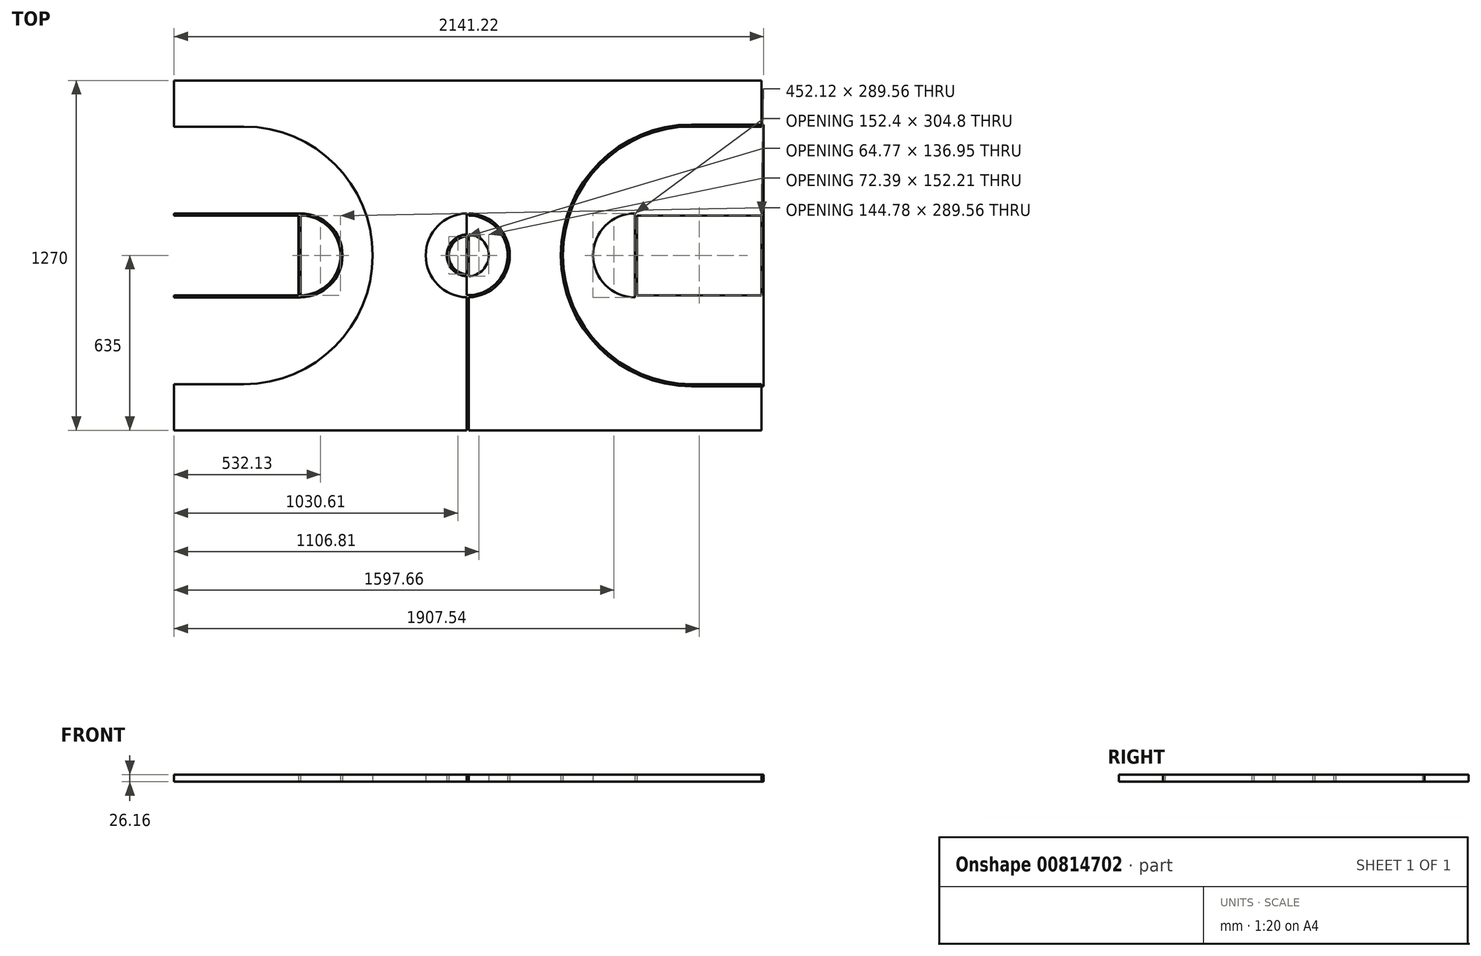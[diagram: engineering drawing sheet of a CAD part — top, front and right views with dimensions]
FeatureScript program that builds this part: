
annotation { "Feature Type Name" : "Feature", "Feature Type Description" : "" }
export const myFeature = defineFeature(function(context is Context, id is Id, definition is map)
    precondition{}
    {
        {
            var Q0;
            Q0=qCreatedBy(makeId("Top.planeOp"),FACE);
            var sketch = newSketch(context, id + "F0", { "sketchPlane" : qUnion([Q0])});
            skLineSegment(sketch, "E0.bottom", {"start": v(-1066.8, -635) * mm, "end": v(1066.8, -635) * mm});
            skLineSegment(sketch, "E0.top", {"start": v(-1066.8, 635) * mm, "end": v(1066.8, 635) * mm});
            skLineSegment(sketch, "E0.left", {"start": v(-1066.8, -635) * mm, "end": v(-1066.8, 635) * mm});
            skLineSegment(sketch, "E0.right", {"start": v(1066.8, -635) * mm, "end": v(1066.8, 635) * mm});
            skPoint(sketch, "E0.middle", {"position": v(0, 0) * mm});
            skLineSegment(sketch, "E1.bottom", {"start": v(-3.81, -635) * mm, "end": v(3.81, -635) * mm});
            skLineSegment(sketch, "E1.top", {"start": v(-3.81, 635) * mm, "end": v(3.81, 635) * mm});
            skLineSegment(sketch, "E1.left", {"start": v(-3.81, -635) * mm, "end": v(-3.81, 635) * mm});
            skLineSegment(sketch, "E1.right", {"start": v(3.81, -635) * mm, "end": v(3.81, 635) * mm});
            skCircle(sketch, "E2", {"center": v(0, 0) * mm, "radius": 152.4 * mm});
            skCircle(sketch, "E3", {"center": v(0, 0) * mm, "radius": 144.78 * mm});
            skCircle(sketch, "E4", {"center": v(0, 0) * mm, "radius": 76.2 * mm});
            skCircle(sketch, "E5", {"center": v(0, 0) * mm, "radius": 68.58 * mm});
            skPoint(sketch, "E6.endSnap0", {"position": v(-1066.8, 0) * mm});
            skLineSegment(sketch, "E7.bottom", {"start": v(-1066.8, -152.4) * mm, "end": v(-607.06, -152.4) * mm});
            skLineSegment(sketch, "E7.top", {"start": v(-1066.8, 152.4) * mm, "end": v(-607.06, 152.4) * mm});
            skLineSegment(sketch, "E7.left", {"start": v(-1066.8, -152.4) * mm, "end": v(-1066.8, 152.4) * mm});
            skLineSegment(sketch, "E7.right", {"start": v(-607.06, -152.4) * mm, "end": v(-607.06, 152.4) * mm});
            skPoint(sketch, "E7.middle", {"position": v(-836.93, 0) * mm});
            skPoint(sketch, "E6.end.orphan", {"position": v(-607.06, 0) * mm});
            skArc(sketch, "E8", {"start": v(-607.06, -152.4) * mm, "mid": v(-454.66, 0) * mm, "end": v(-607.06, 152.4) * mm});
            skLineSegment(sketch, "E9", {"start": v(-1066.8, 635) * mm, "end": v(-1066.8, 474.98) * mm});
            skLineSegment(sketch, "E10", {"start": v(-1066.8, -635) * mm, "end": v(-1066.8, -474.98) * mm});
            skLineSegment(sketch, "E11", {"start": v(-1066.8, 474.98) * mm, "end": v(-812.8, 474.98) * mm});
            skLineSegment(sketch, "E12", {"start": v(-1066.8, -474.98) * mm, "end": v(-812.8, -474.98) * mm});
            skArc(sketch, "E13", {"start": v(-812.8, -474.98) * mm, "mid": v(-337.82, 0) * mm, "end": v(-812.8, 474.98) * mm});
            skLineSegment(sketch, "E14", {"start": v(0, 635) * mm, "end": v(0, -635) * mm});
            skArc(sketch, "E15.MirrorCS", {"start": v(812.8, -474.98) * mm, "mid": v(337.82, 0) * mm, "end": v(812.8, 474.98) * mm});
            skArc(sketch, "E16.MirrorCS", {"start": v(607.06, -152.4) * mm, "mid": v(454.66, 0) * mm, "end": v(607.06, 152.4) * mm});
            skLineSegment(sketch, "E17.MirrorCS", {"start": v(607.06, -152.4) * mm, "end": v(607.06, 152.4) * mm});
            skLineSegment(sketch, "E18.MirrorCS", {"start": v(1066.8, -474.98) * mm, "end": v(812.8, -474.98) * mm});
            skLineSegment(sketch, "E19.MirrorCS", {"start": v(1066.8, 474.98) * mm, "end": v(812.8, 474.98) * mm});
            skLineSegment(sketch, "E20.MirrorCS", {"start": v(1066.8, 152.4) * mm, "end": v(607.06, 152.4) * mm});
            skLineSegment(sketch, "E21.MirrorCS", {"start": v(1066.8, -152.4) * mm, "end": v(607.06, -152.4) * mm});
            skLineSegment(sketch, "E22", {"start": v(-1066.8, 474.98) * mm, "end": v(-1066.8, 467.36) * mm});
            skLineSegment(sketch, "E23", {"start": v(-1066.8, 467.36) * mm, "end": v(-812.8, 467.36) * mm});
            skLineSegment(sketch, "E24", {"start": v(-812.8, 467.36) * mm, "end": v(-812.8, 474.98) * mm});
            skLineSegment(sketch, "E25", {"start": v(-1066.8, -474.98) * mm, "end": v(-1066.8, -467.36) * mm});
            skLineSegment(sketch, "E26", {"start": v(-1066.8, -467.36) * mm, "end": v(-812.8, -467.36) * mm});
            skArc(sketch, "E27", {"start": v(-812.8, -467.36) * mm, "mid": v(-345.44, 0) * mm, "end": v(-812.8, 467.36) * mm});
            skLineSegment(sketch, "E28", {"start": v(-1066.8, 152.4) * mm, "end": v(-1066.8, 144.78) * mm});
            skLineSegment(sketch, "E29", {"start": v(-1066.8, 144.78) * mm, "end": v(-607.06, 144.78) * mm});
            skLineSegment(sketch, "E30", {"start": v(-1066.8, -152.4) * mm, "end": v(-1066.8, -144.78) * mm});
            skLineSegment(sketch, "E31", {"start": v(-1066.8, -144.78) * mm, "end": v(-607.06, -144.78) * mm});
            skLineSegment(sketch, "E32", {"start": v(-607.06, 152.4) * mm, "end": v(-614.68, 152.4) * mm});
            skLineSegment(sketch, "E33", {"start": v(-614.68, 152.4) * mm, "end": v(-614.68, -152.4) * mm});
            skLineSegment(sketch, "E34", {"start": v(-614.68, -152.4) * mm, "end": v(-607.06, -152.4) * mm});
            skArc(sketch, "E35", {"start": v(-607.06, -144.78) * mm, "mid": v(-462.28, 0) * mm, "end": v(-607.06, 144.78) * mm});
            skArc(sketch, "E36.MirrorCS", {"start": v(812.8, -467.36) * mm, "mid": v(345.44, 0) * mm, "end": v(812.8, 467.36) * mm});
            skArc(sketch, "E37.MirrorCS", {"start": v(607.06, -144.78) * mm, "mid": v(462.28, 0) * mm, "end": v(607.06, 144.78) * mm});
            skLineSegment(sketch, "E38.MirrorCS", {"start": v(614.68, 152.4) * mm, "end": v(614.68, -152.4) * mm});
            skLineSegment(sketch, "E39.MirrorCS", {"start": v(1066.8, -144.78) * mm, "end": v(607.06, -144.78) * mm});
            skLineSegment(sketch, "E40.MirrorCS", {"start": v(1066.8, 144.78) * mm, "end": v(607.06, 144.78) * mm});
            skLineSegment(sketch, "E41.MirrorCS", {"start": v(1066.8, -467.36) * mm, "end": v(812.8, -467.36) * mm});
            skLineSegment(sketch, "E42.MirrorCS", {"start": v(1066.8, 467.36) * mm, "end": v(812.8, 467.36) * mm});
            skLineSegment(sketch, "E43", {"start": v(1066.8, 474.98) * mm, "end": v(1074.42, 474.98) * mm});
            skLineSegment(sketch, "E44", {"start": v(1074.42, 474.98) * mm, "end": v(1074.42, -474.98) * mm});
            skLineSegment(sketch, "E45", {"start": v(1074.42, -474.98) * mm, "end": v(1066.8, -474.98) * mm});
            skLineSegment(sketch, "E46.MirrorCS", {"start": v(-1074.42, -474.98) * mm, "end": v(-1066.8, -474.98) * mm});
            skLineSegment(sketch, "E47.MirrorCS", {"start": v(-1074.42, 474.98) * mm, "end": v(-1074.42, -474.98) * mm});
            skLineSegment(sketch, "E48.MirrorCS", {"start": v(-1066.8, 474.98) * mm, "end": v(-1074.42, 474.98) * mm});
            skSolve(sketch);
        }
        {
            var Q0;
            Q0=makeQuery(id+"F0.imprint","IMPRINT",FACE,{"disambiguationData":[TD([[makeQuery(id+"F0.imprint","IMPRINT",EDGE,{"derivedFrom":sQuery(id+"F0.wireOp",EDGE,"E12")}),1.0]])]});
            var Q1;
            Q1=makeQuery(id+"F0.imprint","IMPRINT",FACE,{"disambiguationData":[TD([[makeQuery(id+"F0.imprint","IMPRINT",EDGE,{"derivedFrom":sQuery(id+"F0.wireOp",EDGE,"E11")}),-1.0]])]});
            var Q2;
            {var subQ1=sQuery(id+"F0.wireOp",EDGE,"E29");var subQ6=sQuery(id+"F0.wireOp",EDGE,"E33");var subQ7=makeQuery(id+"F0.imprint","INTERSECT",VERTEX,{"derivedFrom":[subQ1,subQ6]});Q2=makeQuery(id+"F0.imprint","IMPRINT",FACE,{"disambiguationData":[TD([[makeQuery(id+"F0.imprint","IMPRINT",EDGE,{"disambiguationData":[TD([[subQ7,-1.0]])],"derivedFrom":subQ6}),1.0]])]});}
            var Q3;
            {var subQ0=sQuery(id+"F0.wireOp",EDGE,"E7.top");Q3=makeQuery(id+"F0.imprint","IMPRINT",FACE,{"disambiguationData":[TD([[makeQuery(id+"F0.imprint","IMPRINT",EDGE,{"derivedFrom":subQ0}),-1.0]])]});}
            var Q4;
            {var subQ0=sQuery(id+"F0.wireOp",EDGE,"E32");Q4=makeQuery(id+"F0.imprint","IMPRINT",FACE,{"disambiguationData":[TD([[makeQuery(id+"F0.imprint","IMPRINT",EDGE,{"derivedFrom":subQ0}),1.0]])]});}
            var Q5;
            {var subQ0=sQuery(id+"F0.wireOp",EDGE,"E8");Q5=makeQuery(id+"F0.imprint","IMPRINT",FACE,{"disambiguationData":[TD([[makeQuery(id+"F0.imprint","IMPRINT",EDGE,{"derivedFrom":subQ0}),1.0]])]});}
            var Q6;
            {var subQ0=sQuery(id+"F0.wireOp",EDGE,"E7.bottom");Q6=makeQuery(id+"F0.imprint","IMPRINT",FACE,{"disambiguationData":[TD([[makeQuery(id+"F0.imprint","IMPRINT",EDGE,{"derivedFrom":subQ0}),1.0]])]});}
            var Q7;
            {var subQ0=sQuery(id+"F0.wireOp",EDGE,"E34");Q7=makeQuery(id+"F0.imprint","IMPRINT",FACE,{"disambiguationData":[TD([[makeQuery(id+"F0.imprint","IMPRINT",EDGE,{"derivedFrom":subQ0}),1.0]])]});}
            var Q8;
            {var subQ0=sQuery(id+"F0.wireOp",EDGE,"E4");var subQ1=sQuery(id+"F0.wireOp",EDGE,"E1.left");var subQ2=makeQuery(id+"F0.imprint","INTERSECT",VERTEX,{"disambiguationData":[OD(0.0)],"derivedFrom":[subQ1,subQ0]});Q8=makeQuery(id+"F0.imprint","IMPRINT",FACE,{"disambiguationData":[TD([[makeQuery(id+"F0.imprint","IMPRINT",EDGE,{"disambiguationData":[TD([[subQ2,-1.0]])],"derivedFrom":subQ1}),1.0]])]});}
            var Q9;
            {var subQ0=sQuery(id+"F0.wireOp",EDGE,"E4");var subQ1=sQuery(id+"F0.wireOp",EDGE,"E1.right");var subQ2=makeQuery(id+"F0.imprint","INTERSECT",VERTEX,{"disambiguationData":[OD(0.0)],"derivedFrom":[subQ1,subQ0]});Q9=makeQuery(id+"F0.imprint","IMPRINT",FACE,{"disambiguationData":[TD([[makeQuery(id+"F0.imprint","IMPRINT",EDGE,{"disambiguationData":[TD([[subQ2,-1.0]])],"derivedFrom":subQ1}),-1.0]])]});}
            var Q10;
            {var subQ0=sQuery(id+"F0.wireOp",EDGE,"E5");var subQ1=sQuery(id+"F0.wireOp",EDGE,"E1.right");var subQ2=makeQuery(id+"F0.imprint","INTERSECT",VERTEX,{"disambiguationData":[OD(1.0)],"derivedFrom":[subQ1,subQ0]});Q10=makeQuery(id+"F0.imprint","IMPRINT",FACE,{"disambiguationData":[TD([[makeQuery(id+"F0.imprint","IMPRINT",EDGE,{"disambiguationData":[TD([[subQ2,-1.0]])],"derivedFrom":subQ1}),1.0]])]});}
            var Q11;
            {var subQ0=sQuery(id+"F0.wireOp",EDGE,"E5");var subQ1=sQuery(id+"F0.wireOp",EDGE,"E1.left");var subQ2=makeQuery(id+"F0.imprint","INTERSECT",VERTEX,{"disambiguationData":[OD(1.0)],"derivedFrom":[subQ1,subQ0]});Q11=makeQuery(id+"F0.imprint","IMPRINT",FACE,{"disambiguationData":[TD([[makeQuery(id+"F0.imprint","IMPRINT",EDGE,{"disambiguationData":[TD([[subQ2,-1.0]])],"derivedFrom":subQ1}),-1.0]])]});}
            var Q12;
            {var subQ0=sQuery(id+"F0.wireOp",EDGE,"E2");var subQ1=sQuery(id+"F0.wireOp",EDGE,"E1.left");var subQ2=makeQuery(id+"F0.imprint","INTERSECT",VERTEX,{"disambiguationData":[OD(0.0)],"derivedFrom":[subQ1,subQ0]});Q12=makeQuery(id+"F0.imprint","IMPRINT",FACE,{"disambiguationData":[TD([[makeQuery(id+"F0.imprint","IMPRINT",EDGE,{"disambiguationData":[TD([[subQ2,-1.0]])],"derivedFrom":subQ1}),1.0]])]});}
            var Q13;
            {var subQ0=sQuery(id+"F0.wireOp",EDGE,"E3");var subQ1=sQuery(id+"F0.wireOp",EDGE,"E1.left");var subQ2=makeQuery(id+"F0.imprint","INTERSECT",VERTEX,{"disambiguationData":[OD(1.0)],"derivedFrom":[subQ1,subQ0]});Q13=makeQuery(id+"F0.imprint","IMPRINT",FACE,{"disambiguationData":[TD([[makeQuery(id+"F0.imprint","IMPRINT",EDGE,{"disambiguationData":[TD([[subQ2,-1.0]])],"derivedFrom":subQ1}),-1.0]])]});}
            var Q14;
            {var subQ0=sQuery(id+"F0.wireOp",EDGE,"E3");var subQ1=sQuery(id+"F0.wireOp",EDGE,"E1.right");var subQ2=makeQuery(id+"F0.imprint","INTERSECT",VERTEX,{"disambiguationData":[OD(1.0)],"derivedFrom":[subQ1,subQ0]});Q14=makeQuery(id+"F0.imprint","IMPRINT",FACE,{"disambiguationData":[TD([[makeQuery(id+"F0.imprint","IMPRINT",EDGE,{"disambiguationData":[TD([[subQ2,-1.0]])],"derivedFrom":subQ1}),1.0]])]});}
            var Q15;
            {var subQ0=sQuery(id+"F0.wireOp",EDGE,"E2");var subQ1=sQuery(id+"F0.wireOp",EDGE,"E1.right");var subQ2=makeQuery(id+"F0.imprint","INTERSECT",VERTEX,{"disambiguationData":[OD(0.0)],"derivedFrom":[subQ1,subQ0]});Q15=makeQuery(id+"F0.imprint","IMPRINT",FACE,{"disambiguationData":[TD([[makeQuery(id+"F0.imprint","IMPRINT",EDGE,{"disambiguationData":[TD([[subQ2,-1.0]])],"derivedFrom":subQ1}),-1.0]])]});}
            var Q16;
            {var subQ0=sQuery(id+"F0.wireOp",EDGE,"E4");var subQ1=sQuery(id+"F0.wireOp",EDGE,"E1.left");var subQ2=makeQuery(id+"F0.imprint","INTERSECT",VERTEX,{"disambiguationData":[OD(0.0)],"derivedFrom":[subQ1,subQ0]});Q16=makeQuery(id+"F0.imprint","IMPRINT",FACE,{"disambiguationData":[TD([[makeQuery(id+"F0.imprint","IMPRINT",EDGE,{"disambiguationData":[TD([[subQ2,-1.0]])],"derivedFrom":subQ1}),-1.0]])]});}
            var Q17;
            {var subQ0=sQuery(id+"F0.wireOp",EDGE,"E4");var subQ1=sQuery(id+"F0.wireOp",EDGE,"E1.right");var subQ2=makeQuery(id+"F0.imprint","INTERSECT",VERTEX,{"disambiguationData":[OD(0.0)],"derivedFrom":[subQ1,subQ0]});Q17=makeQuery(id+"F0.imprint","IMPRINT",FACE,{"disambiguationData":[TD([[makeQuery(id+"F0.imprint","IMPRINT",EDGE,{"disambiguationData":[TD([[subQ2,-1.0]])],"derivedFrom":subQ1}),1.0]])]});}
            var Q18;
            {var subQ0=sQuery(id+"F0.wireOp",EDGE,"E2");var subQ1=sQuery(id+"F0.wireOp",EDGE,"E1.left");var subQ2=makeQuery(id+"F0.imprint","INTERSECT",VERTEX,{"disambiguationData":[OD(0.0)],"derivedFrom":[subQ1,subQ0]});Q18=makeQuery(id+"F0.imprint","IMPRINT",FACE,{"disambiguationData":[TD([[makeQuery(id+"F0.imprint","IMPRINT",EDGE,{"disambiguationData":[TD([[subQ2,-1.0]])],"derivedFrom":subQ1}),-1.0]])]});}
            var Q19;
            {var subQ0=sQuery(id+"F0.wireOp",EDGE,"E2");var subQ1=sQuery(id+"F0.wireOp",EDGE,"E1.right");var subQ2=makeQuery(id+"F0.imprint","INTERSECT",VERTEX,{"disambiguationData":[OD(0.0)],"derivedFrom":[subQ1,subQ0]});Q19=makeQuery(id+"F0.imprint","IMPRINT",FACE,{"disambiguationData":[TD([[makeQuery(id+"F0.imprint","IMPRINT",EDGE,{"disambiguationData":[TD([[subQ2,-1.0]])],"derivedFrom":subQ1}),1.0]])]});}
            var Q20;
            Q20=makeQuery(id+"F0.imprint","IMPRINT",FACE,{"disambiguationData":[TD([[makeQuery(id+"F0.imprint","IMPRINT",EDGE,{"derivedFrom":sQuery(id+"F0.wireOp",EDGE,"E15.MirrorCS")}),-1.0]])]});
            var Q21;
            {var subQ0=sQuery(id+"F0.wireOp",EDGE,"E20.MirrorCS");var subQ1=sQuery(id+"F0.wireOp",EDGE,"E0.right");var subQ2=makeQuery(id+"F0.imprint","INTERSECT",VERTEX,{"derivedFrom":[subQ1,subQ0]});Q21=makeQuery(id+"F0.imprint","IMPRINT",FACE,{"disambiguationData":[TD([[makeQuery(id+"F0.imprint","IMPRINT",EDGE,{"disambiguationData":[TD([[subQ2,1.0]])],"derivedFrom":subQ1}),1.0]])]});}
            var Q22;
            {var subQ0=sQuery(id+"F0.wireOp",EDGE,"E20.MirrorCS");var subQ5=sQuery(id+"F0.wireOp",EDGE,"E38.MirrorCS");var subQ6=makeQuery(id+"F0.imprint","INTERSECT",VERTEX,{"derivedFrom":[subQ0,subQ5]});Q22=makeQuery(id+"F0.imprint","IMPRINT",FACE,{"disambiguationData":[TD([[makeQuery(id+"F0.imprint","IMPRINT",EDGE,{"disambiguationData":[TD([[subQ6,-1.0]])],"derivedFrom":subQ5}),-1.0]])]});}
            var Q23;
            {var subQ4=sQuery(id+"F0.wireOp",EDGE,"E40.MirrorCS");var subQ6=sQuery(id+"F0.wireOp",EDGE,"E38.MirrorCS");var subQ7=makeQuery(id+"F0.imprint","INTERSECT",VERTEX,{"derivedFrom":[subQ6,subQ4]});Q23=makeQuery(id+"F0.imprint","IMPRINT",FACE,{"disambiguationData":[TD([[makeQuery(id+"F0.imprint","IMPRINT",EDGE,{"disambiguationData":[TD([[subQ7,-1.0]])],"derivedFrom":subQ6}),-1.0]])]});}
            var Q24;
            {var subQ0=sQuery(id+"F0.wireOp",EDGE,"E16.MirrorCS");Q24=makeQuery(id+"F0.imprint","IMPRINT",FACE,{"disambiguationData":[TD([[makeQuery(id+"F0.imprint","IMPRINT",EDGE,{"derivedFrom":subQ0}),-1.0]])]});}
            var Q25;
            {var subQ0=sQuery(id+"F0.wireOp",EDGE,"E21.MirrorCS");var subQ1=sQuery(id+"F0.wireOp",EDGE,"E0.right");var subQ2=makeQuery(id+"F0.imprint","INTERSECT",VERTEX,{"derivedFrom":[subQ1,subQ0]});Q25=makeQuery(id+"F0.imprint","IMPRINT",FACE,{"disambiguationData":[TD([[makeQuery(id+"F0.imprint","IMPRINT",EDGE,{"disambiguationData":[TD([[subQ2,-1.0]])],"derivedFrom":subQ1}),1.0]])]});}
            var Q26;
            {var subQ0=sQuery(id+"F0.wireOp",EDGE,"E21.MirrorCS");var subQ5=sQuery(id+"F0.wireOp",EDGE,"E38.MirrorCS");var subQ6=makeQuery(id+"F0.imprint","INTERSECT",VERTEX,{"derivedFrom":[subQ0,subQ5]});Q26=makeQuery(id+"F0.imprint","IMPRINT",FACE,{"disambiguationData":[TD([[makeQuery(id+"F0.imprint","IMPRINT",EDGE,{"disambiguationData":[TD([[subQ6,1.0]])],"derivedFrom":subQ5}),-1.0]])]});}
            var Q27;
            {var subQ8=sQuery(id+"F0.wireOp",EDGE,"E43");Q27=makeQuery(id+"F0.imprint","IMPRINT",FACE,{"disambiguationData":[TD([[makeQuery(id+"F0.imprint","IMPRINT",EDGE,{"derivedFrom":subQ8}),-1.0]])]});}
            var Q28;
            Q28=makeQuery(id+"F0.imprint","IMPRINT",FACE,{"disambiguationData":[TD([[makeQuery(id+"F0.imprint","IMPRINT",EDGE,{"derivedFrom":sQuery(id+"F0.wireOp",EDGE,"E7.left")}),1.0]])]});
            var Q29;
            {var subQ0=sQuery(id+"F0.wireOp",EDGE,"E1.left");var subQ5=sQuery(id+"F0.wireOp",EDGE,"E2");var subQ6=makeQuery(id+"F0.imprint","INTERSECT",VERTEX,{"disambiguationData":[OD(1.0)],"derivedFrom":[subQ0,subQ5]});Q29=makeQuery(id+"F0.imprint","IMPRINT",FACE,{"disambiguationData":[TD([[makeQuery(id+"F0.imprint","IMPRINT",EDGE,{"disambiguationData":[TD([[subQ6,1.0]])],"derivedFrom":subQ5}),-1.0]])]});}
            var Q30;
            {var subQ0=sQuery(id+"F0.wireOp",EDGE,"E1.right");var subQ5=sQuery(id+"F0.wireOp",EDGE,"E2");var subQ7=makeQuery(id+"F0.imprint","INTERSECT",VERTEX,{"disambiguationData":[OD(1.0)],"derivedFrom":[subQ0,subQ5]});Q30=makeQuery(id+"F0.imprint","IMPRINT",FACE,{"disambiguationData":[TD([[makeQuery(id+"F0.imprint","IMPRINT",EDGE,{"disambiguationData":[TD([[subQ7,-1.0]])],"derivedFrom":subQ5}),-1.0]])]});}
            var Q31;
            {var subQ0=sQuery(id+"F0.wireOp",EDGE,"E4");var subQ1=sQuery(id+"F0.wireOp",EDGE,"E1.left");var subQ2=makeQuery(id+"F0.imprint","INTERSECT",VERTEX,{"disambiguationData":[OD(1.0)],"derivedFrom":[subQ1,subQ0]});Q31=makeQuery(id+"F0.imprint","IMPRINT",FACE,{"disambiguationData":[TD([[makeQuery(id+"F0.imprint","IMPRINT",EDGE,{"disambiguationData":[TD([[subQ2,-1.0]])],"derivedFrom":subQ1}),-1.0]])]});}
            var Q32;
            {var subQ0=sQuery(id+"F0.wireOp",EDGE,"E4");var subQ1=sQuery(id+"F0.wireOp",EDGE,"E1.right");var subQ2=makeQuery(id+"F0.imprint","INTERSECT",VERTEX,{"disambiguationData":[OD(1.0)],"derivedFrom":[subQ1,subQ0]});Q32=makeQuery(id+"F0.imprint","IMPRINT",FACE,{"disambiguationData":[TD([[makeQuery(id+"F0.imprint","IMPRINT",EDGE,{"disambiguationData":[TD([[subQ2,-1.0]])],"derivedFrom":subQ1}),1.0]])]});}
            var Q33;
            {var subQ0=sQuery(id+"F0.wireOp",EDGE,"E5");var subQ1=sQuery(id+"F0.wireOp",EDGE,"E1.left");var subQ2=makeQuery(id+"F0.imprint","INTERSECT",VERTEX,{"disambiguationData":[OD(0.0)],"derivedFrom":[subQ1,subQ0]});Q33=makeQuery(id+"F0.imprint","IMPRINT",FACE,{"disambiguationData":[TD([[makeQuery(id+"F0.imprint","IMPRINT",EDGE,{"disambiguationData":[TD([[subQ2,-1.0]])],"derivedFrom":subQ1}),-1.0]])]});}
            var Q34;
            {var subQ0=sQuery(id+"F0.wireOp",EDGE,"E5");var subQ1=sQuery(id+"F0.wireOp",EDGE,"E1.right");var subQ2=makeQuery(id+"F0.imprint","INTERSECT",VERTEX,{"disambiguationData":[OD(0.0)],"derivedFrom":[subQ1,subQ0]});Q34=makeQuery(id+"F0.imprint","IMPRINT",FACE,{"disambiguationData":[TD([[makeQuery(id+"F0.imprint","IMPRINT",EDGE,{"disambiguationData":[TD([[subQ2,-1.0]])],"derivedFrom":subQ1}),1.0]])]});}
            var Q35;
            {var subQ0=sQuery(id+"F0.wireOp",EDGE,"E3");var subQ1=sQuery(id+"F0.wireOp",EDGE,"E1.left");var subQ2=makeQuery(id+"F0.imprint","INTERSECT",VERTEX,{"disambiguationData":[OD(0.0)],"derivedFrom":[subQ1,subQ0]});Q35=makeQuery(id+"F0.imprint","IMPRINT",FACE,{"disambiguationData":[TD([[makeQuery(id+"F0.imprint","IMPRINT",EDGE,{"disambiguationData":[TD([[subQ2,-1.0]])],"derivedFrom":subQ1}),-1.0]])]});}
            var Q36;
            {var subQ0=sQuery(id+"F0.wireOp",EDGE,"E3");var subQ1=sQuery(id+"F0.wireOp",EDGE,"E1.right");var subQ2=makeQuery(id+"F0.imprint","INTERSECT",VERTEX,{"disambiguationData":[OD(0.0)],"derivedFrom":[subQ1,subQ0]});Q36=makeQuery(id+"F0.imprint","IMPRINT",FACE,{"disambiguationData":[TD([[makeQuery(id+"F0.imprint","IMPRINT",EDGE,{"disambiguationData":[TD([[subQ2,-1.0]])],"derivedFrom":subQ1}),1.0]])]});}
            var Q37;
            {var subQ0=sQuery(id+"F0.wireOp",EDGE,"E1.left");var subQ5=sQuery(id+"F0.wireOp",EDGE,"E2");var subQ6=makeQuery(id+"F0.imprint","INTERSECT",VERTEX,{"disambiguationData":[OD(0.0)],"derivedFrom":[subQ0,subQ5]});Q37=makeQuery(id+"F0.imprint","IMPRINT",FACE,{"disambiguationData":[TD([[makeQuery(id+"F0.imprint","IMPRINT",EDGE,{"disambiguationData":[TD([[subQ6,-1.0]])],"derivedFrom":subQ5}),-1.0]])]});}
            var Q38;
            {var subQ0=sQuery(id+"F0.wireOp",EDGE,"E1.right");var subQ5=sQuery(id+"F0.wireOp",EDGE,"E2");var subQ6=makeQuery(id+"F0.imprint","INTERSECT",VERTEX,{"disambiguationData":[OD(0.0)],"derivedFrom":[subQ0,subQ5]});Q38=makeQuery(id+"F0.imprint","IMPRINT",FACE,{"disambiguationData":[TD([[makeQuery(id+"F0.imprint","IMPRINT",EDGE,{"disambiguationData":[TD([[subQ6,1.0]])],"derivedFrom":subQ5}),-1.0]])]});}
            extrude(context, id + "F1", {"entities" : qUnion([Q0, Q1, Q2, Q3, Q4, Q5, Q6, Q7, Q8, Q9, Q10, Q11, Q12, Q13, Q14, Q15, Q16, Q17, Q18, Q19, Q20, Q21, Q22, Q23, Q24, Q25, Q26, Q27, Q28, Q29, Q30, Q31, Q32, Q33, Q34, Q35, Q36, Q37, Q38]), "depth" : 0.76 * mm, "offsetDistance" : 25.4 * mm});
        }
        {
            var Q0;
            Q0=makeQuery(id+"F1.opExtrude","CAP_FACE",FACE,{"disambiguationData":[OSD([sQuery(id+"F0.wireOp",EDGE,"E0.left"),sQuery(id+"F0.wireOp",EDGE,"E7.bottom"),sQuery(id+"F0.wireOp",EDGE,"E7.top"),sQuery(id+"F0.wireOp",EDGE,"E7.left"),sQuery(id+"F0.wireOp",EDGE,"E7.right"),sQuery(id+"F0.wireOp",EDGE,"E8"),sQuery(id+"F0.wireOp",EDGE,"E11"),sQuery(id+"F0.wireOp",EDGE,"E12"),sQuery(id+"F0.wireOp",EDGE,"E13"),sQuery(id+"F0.wireOp",EDGE,"E23"),sQuery(id+"F0.wireOp",EDGE,"E26"),sQuery(id+"F0.wireOp",EDGE,"E27"),sQuery(id+"F0.wireOp",EDGE,"E29"),sQuery(id+"F0.wireOp",EDGE,"E31"),sQuery(id+"F0.wireOp",EDGE,"E32"),sQuery(id+"F0.wireOp",EDGE,"E33"),sQuery(id+"F0.wireOp",EDGE,"E34"),sQuery(id+"F0.wireOp",EDGE,"E35"),sQuery(id+"F0.wireOp",EDGE,"E46.MirrorCS"),sQuery(id+"F0.wireOp",EDGE,"E47.MirrorCS"),sQuery(id+"F0.wireOp",EDGE,"E48.MirrorCS")])],"isStart":false});
            extrude(context, id + "F2", {"entities" : qUnion([Q0]), "operationType" : NewBodyOperationType.ADD, "depth" : 25.4 * mm, "offsetDistance" : 25.4 * mm});
        }
        {
            var Q0;
            Q0=makeQuery(id+"F1.opExtrude","CAP_FACE",FACE,{"disambiguationData":[OSD([sQuery(id+"F0.wireOp",EDGE,"E1.bottom"),sQuery(id+"F0.wireOp",EDGE,"E1.top"),sQuery(id+"F0.wireOp",EDGE,"E1.left"),sQuery(id+"F0.wireOp",EDGE,"E1.right"),sQuery(id+"F0.wireOp",EDGE,"E2"),sQuery(id+"F0.wireOp",EDGE,"E3"),sQuery(id+"F0.wireOp",EDGE,"E4"),sQuery(id+"F0.wireOp",EDGE,"E5")])],"isStart":false});
            extrude(context, id + "F3", {"entities" : qUnion([Q0]), "operationType" : NewBodyOperationType.ADD, "depth" : 25.4 * mm, "offsetDistance" : 25.4 * mm});
        }
        {
            var Q0;
            Q0=makeQuery(id+"F1.opExtrude","CAP_FACE",FACE,{"disambiguationData":[OSD([sQuery(id+"F0.wireOp",EDGE,"E0.right"),sQuery(id+"F0.wireOp",EDGE,"E15.MirrorCS"),sQuery(id+"F0.wireOp",EDGE,"E16.MirrorCS"),sQuery(id+"F0.wireOp",EDGE,"E17.MirrorCS"),sQuery(id+"F0.wireOp",EDGE,"E18.MirrorCS"),sQuery(id+"F0.wireOp",EDGE,"E19.MirrorCS"),sQuery(id+"F0.wireOp",EDGE,"E20.MirrorCS"),sQuery(id+"F0.wireOp",EDGE,"E21.MirrorCS"),sQuery(id+"F0.wireOp",EDGE,"E36.MirrorCS"),sQuery(id+"F0.wireOp",EDGE,"E37.MirrorCS"),sQuery(id+"F0.wireOp",EDGE,"E38.MirrorCS"),sQuery(id+"F0.wireOp",EDGE,"E39.MirrorCS"),sQuery(id+"F0.wireOp",EDGE,"E40.MirrorCS"),sQuery(id+"F0.wireOp",EDGE,"E41.MirrorCS"),sQuery(id+"F0.wireOp",EDGE,"E42.MirrorCS"),sQuery(id+"F0.wireOp",EDGE,"E43"),sQuery(id+"F0.wireOp",EDGE,"E44"),sQuery(id+"F0.wireOp",EDGE,"E45")])],"isStart":false});
            extrude(context, id + "F4", {"entities" : qUnion([Q0]), "operationType" : NewBodyOperationType.ADD, "depth" : 25.4 * mm, "offsetDistance" : 25.4 * mm});
        }
    });
